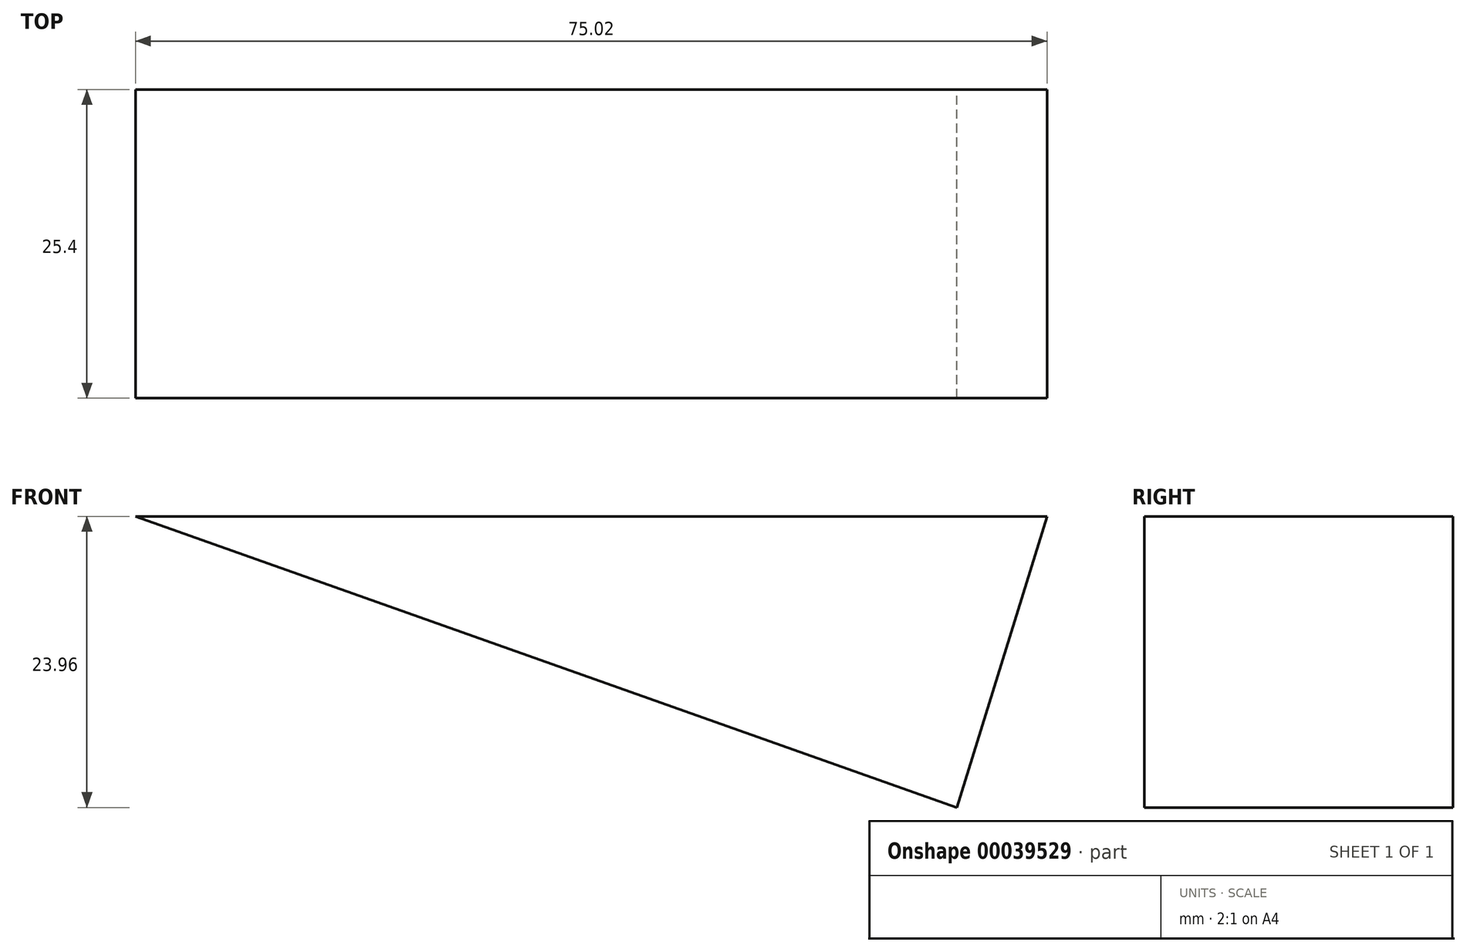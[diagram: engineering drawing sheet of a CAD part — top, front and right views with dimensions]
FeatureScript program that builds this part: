
annotation { "Feature Type Name" : "Feature", "Feature Type Description" : "" }
export const myFeature = defineFeature(function(context is Context, id is Id, definition is map)
    precondition{}
    {
        {
            var Q0;
            Q0=qCreatedBy(makeId("Front.planeOp"),FACE);
            var sketch = newSketch(context, id + "F0", { "sketchPlane" : qUnion([Q0])});
            skLineSegment(sketch, "E0", {"start": v(-31.1, 58.9) * mm, "end": v(43.93, 58.9) * mm});
            skLineSegment(sketch, "E1", {"start": v(43.93, 58.9) * mm, "end": v(36.51, 34.94) * mm});
            skLineSegment(sketch, "E2", {"start": v(36.51, 34.94) * mm, "end": v(-31.1, 58.9) * mm});
            skSolve(sketch);
        }
        {
            var Q0;
            Q0=makeQuery(id+"F0.imprint","IMPRINT",FACE,{"disambiguationData":[TD([[makeQuery(id+"F0.imprint","IMPRINT",EDGE,{"derivedFrom":sQuery(id+"F0.wireOp",EDGE,"E0")}),-1.0]])]});
            extrude(context, id + "F1", {"entities" : qUnion([Q0]), "depth" : 25.4 * mm});
        }
    });
